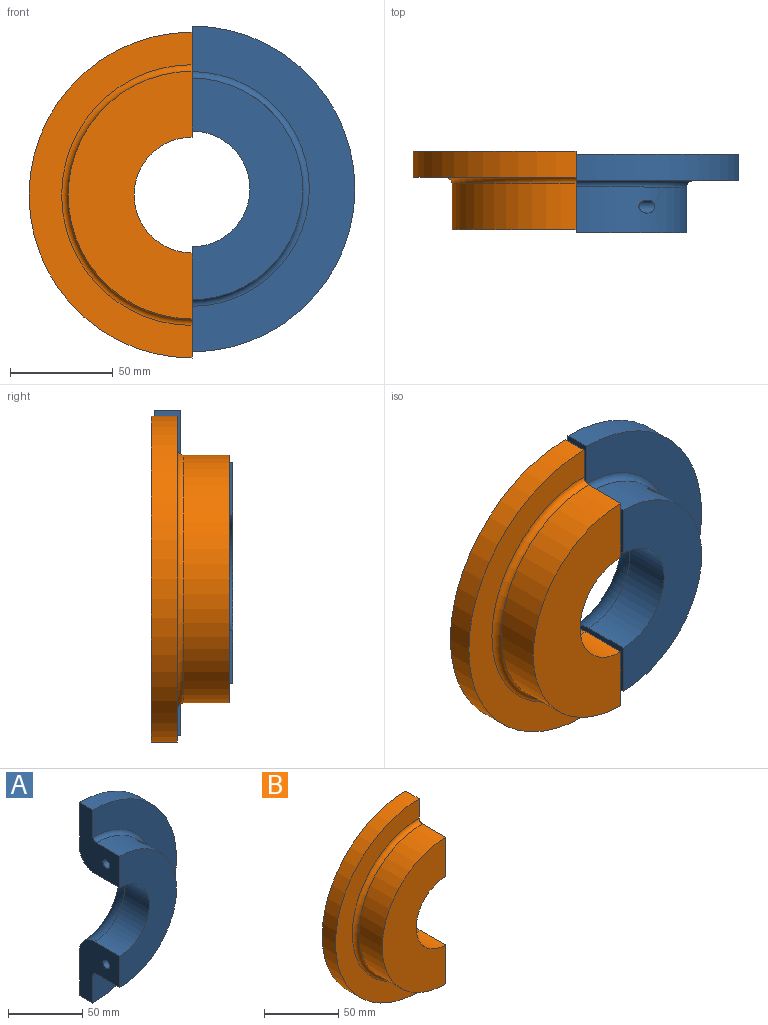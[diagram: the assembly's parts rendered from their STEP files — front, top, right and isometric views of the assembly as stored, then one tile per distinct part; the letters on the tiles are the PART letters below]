
ASSEMBLY  parts=2 mates=1
PART A: 12 faces, bbox 79.4x38.1x158.8 mm
  f0: cylinder r=53.98mm len=107.95mm, axis (0,1,0), area 3670mm2, adj f4,f7,f8,f9,f10,f11
  f1: cylinder r=79.38mm len=158.75mm, axis (0,1,0), area 3166.9mm2, adj f2,f3,f8,f9
  f2: plane 158.75x79.38mm, normal (0,-1,0), area 4766.2mm2, adj f1,f7,f8,f9
  f3: plane 158.75x79.38mm, normal (0,1,0), area 7061.8mm2, adj f1,f6,f8,f9
  f4: plane 107.95x53.98mm, normal (0,-1,0), area 3327.6mm2, adj f0,f5,f8,f9
  f5: cylinder r=28.19mm len=56.39mm, axis (0,-1,0), area 2109.2mm2, adj f4,f6,f8,f9
  f6: torus R=42.48mm, axis (0,-1,0), area 2353.9mm2, adj f3,f5,f8,f9
  f7: torus R=57.15mm, axis (0,-1,0), area 863.8mm2, adj f0,f2,f8,f9
  f8: plane 51.18x38.1mm, normal (-1,0,0), area 1231.5mm2, adj f0,f1,f2,f3,f4,f5,f6,f7
  f9: plane 51.18x38.1mm, normal (-1,0,0), area 1231.5mm2, adj f0,f1,f2,f3,f4,f5,f6,f7
  f10: cylinder r=3.17mm len=38.23mm, axis (-1,0,0), area 690.3mm2, adj f0,f9
  f11: cylinder r=3.17mm len=38.23mm, axis (-1,0,0), area 690.3mm2, adj f0,f8
PART B: 14 faces, bbox 79.4x38.1x158.8 mm
  f0: cylinder r=79.38mm len=158.75mm, axis (0,1,0), area 3166.9mm2, adj f1,f2,f8,f9
  f1: plane 158.75x79.38mm, normal (0,-1,0), area 3562.8mm2, adj f0,f7,f8,f9
  f2: plane 158.75x79.38mm, normal (0,1,0), area 7061.8mm2, adj f0,f6,f8,f9
  f3: cylinder r=60.32mm len=120.65mm, axis (0,1,0), area 4212mm2, adj f4,f7,f8,f9
  f4: plane 120.65x60.33mm, normal (0,-1,0), area 4467.7mm2, adj f3,f5,f8,f9
  f5: cylinder r=28.19mm len=56.39mm, axis (0,-1,0), area 2109.2mm2, adj f4,f6,f8,f9
  f6: torus R=42.48mm, axis (0,-1,0), area 2353.9mm2, adj f2,f5,f8,f9
  f7: torus R=63.5mm, axis (0,-1,0), area 963.2mm2, adj f1,f3,f8,f9
  f8: plane 51.18x38.1mm, normal (1,0,0), area 1404mm2, adj f0,f1,f2,f3,f4,f5,f6,f7
  f9: plane 51.18x38.1mm, normal (1,0,0), area 1404mm2, adj f0,f1,f2,f3,f4,f5,f6,f7
  f10: cone r=0mm half-angle=59deg, axis (1,0,0), area 23.9mm2, adj f11
  f11: cylinder r=2.55mm len=25.4mm, axis (1,0,0), area 407.4mm2, adj f9,f10
  f12: cone r=0mm half-angle=59deg, axis (1,0,0), area 23.9mm2, adj f13
  f13: cylinder r=2.55mm len=25.4mm, axis (1,0,0), area 407.4mm2, adj f8,f12
PLACE A t=(-75.59,-3.37,-3.52)mm
PLACE B t=(-75.59,-1.78,-6.51)mm
MATE cylindrical B.f10 <-> A.f10  axis (1,0,0) through (-75.59,-28.77,37.75)mm
